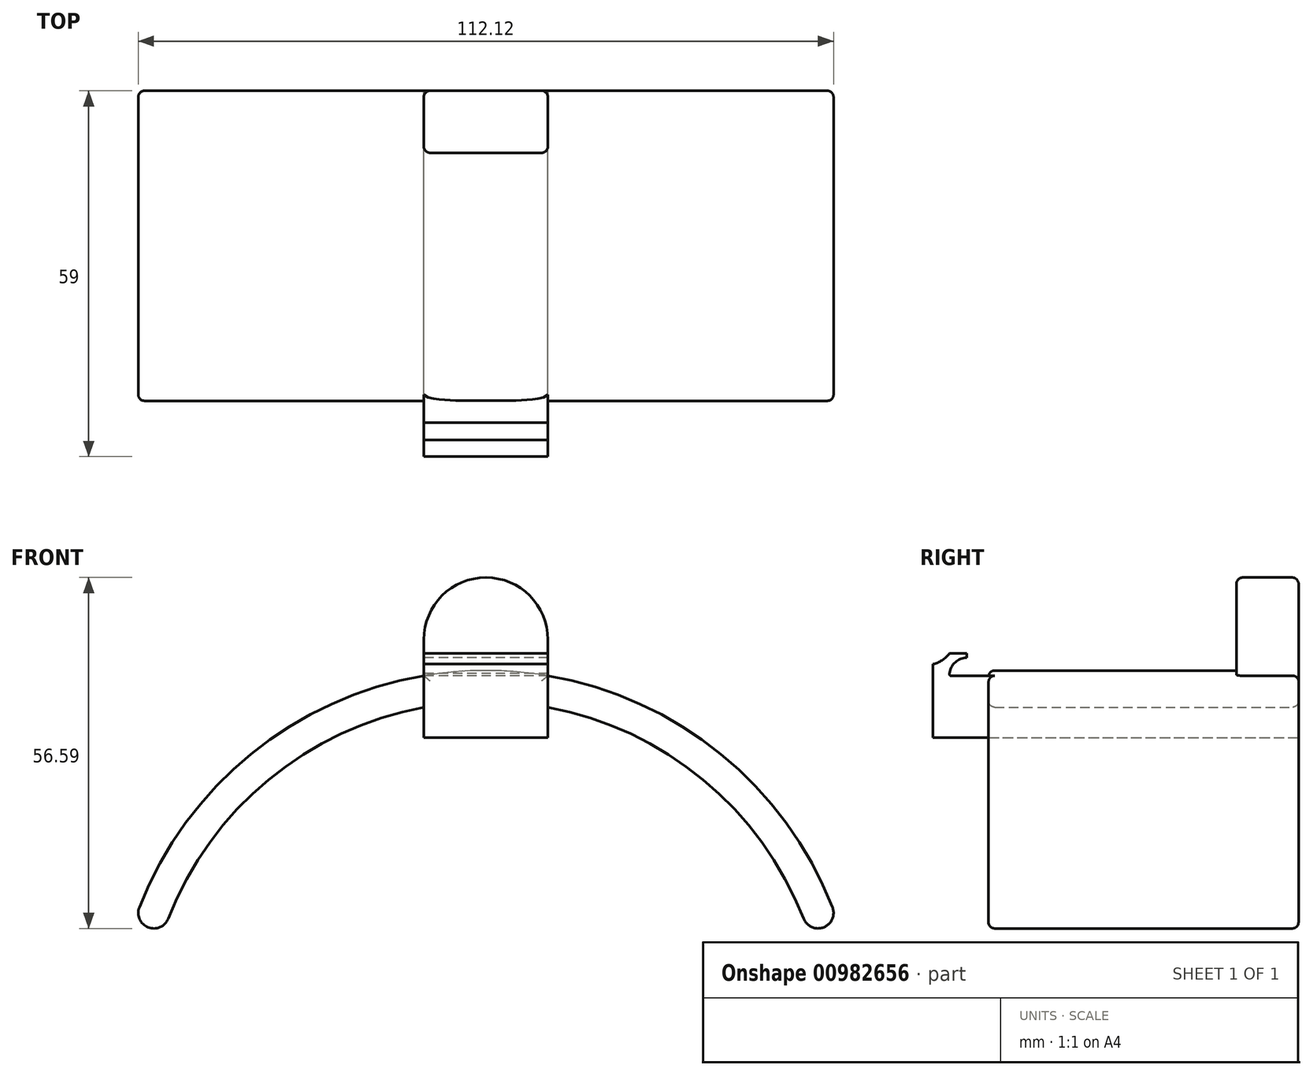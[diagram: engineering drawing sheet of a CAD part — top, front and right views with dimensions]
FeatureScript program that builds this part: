
annotation { "Feature Type Name" : "Feature", "Feature Type Description" : "" }
export const myFeature = defineFeature(function(context is Context, id is Id, definition is map)
    precondition{}
    {
        {
            var Q0;
            Q0=qCreatedBy(makeId("Right.planeOp"),FACE);
            var sketch = newSketch(context, id + "F0", { "sketchPlane" : qUnion([Q0])});
            skLineSegment(sketch, "E0.bottom", {"start": v(2.7, 2.31) * mm, "end": v(5.5, 2.31) * mm});
            skLineSegment(sketch, "E0.right", {"start": v(5.5, 2.31) * mm, "end": v(5.5, 1.65) * mm});
            skLineSegment(sketch, "E1", {"start": v(2.7, -1.07) * mm, "end": v(2.7, -0.9) * mm});
            skLineSegment(sketch, "E2.top", {"start": v(0, -11.29) * mm, "end": v(9, -11.29) * mm});
            skLineSegment(sketch, "E2.right", {"start": v(9, -1.29) * mm, "end": v(9, -11.29) * mm});
            skLineSegment(sketch, "E3", {"start": v(2.92, -1.29) * mm, "end": v(9, -1.29) * mm});
            skArc(sketch, "E4", {"start": v(0, 0.58) * mm, "mid": v(1.5, 1.2) * mm, "end": v(2.7, 2.31) * mm});
            skPoint(sketch, "E5.visualSharp", {"position": v(2.7, -1.29) * mm});
            skArc(sketch, "E5.filletArc", {"start": v(2.7, -1.07) * mm, "mid": v(2.76, -1.22) * mm, "end": v(2.92, -1.29) * mm});
            skArc(sketch, "E6", {"start": v(5.5, 1.65) * mm, "mid": v(3.63, 0.89) * mm, "end": v(2.7, -0.9) * mm});
            skLineSegment(sketch, "E7", {"start": v(0, 0.58) * mm, "end": v(0, -11.29) * mm});
            skLineSegment(sketch, "E8", {"start": v(2.7, -0.9) * mm, "end": v(2.7, 6.55) * mm, "construction": true});
            skSolve(sketch);
        }
        {
            var Q0;
            Q0=qSketchRegion(id+"F0",true);
            extrude(context, id + "F1", {"entities" : qUnion([Q0]), "depth" : 20 * mm, "offsetDistance" : 25.4 * mm});
        }
        {
            var Q0;
            Q0=qCreatedBy(makeId("Right.planeOp"),FACE);
            var sketch = newSketch(context, id + "F2", { "sketchPlane" : qUnion([Q0])});
            skLineSegment(sketch, "E9.top", {"start": v(9, -1.29) * mm, "end": v(59, -1.29) * mm});
            skLineSegment(sketch, "E9.right", {"start": v(59, -11.29) * mm, "end": v(59, -1.29) * mm});
            skPoint(sketch, "E10", {"position": v(9, -11.29) * mm});
            skLineSegment(sketch, "E11", {"start": v(59, -11.29) * mm, "end": v(9, -11.29) * mm});
            skLineSegment(sketch, "E12", {"start": v(9, -11.29) * mm, "end": v(9, -1.29) * mm});
            skSolve(sketch);
        }
        {
            var Q0;
            Q0 = qSketchRegion(id + "F2", true);
            extrude(context, id + "F3", {"entities" : qUnion([Q0]), "operationType" : NewBodyOperationType.ADD, "depth" : 20 * mm, "offsetDistance" : 25.4 * mm});
        }
        {
            var Q0;
            Q0=makeQuery(id+"F3.opExtrude","SWEPT_FACE",FACE,{"disambiguationData":[OSD([sQuery(id+"F2.wireOp",EDGE,"E9.right")])]});
            cPlane(context, id + "F4", {"entities" : qUnion([Q0]), "cplaneType" : CPlaneType.OFFSET, "offset" : 0 * mm, "width" : 152.4 * mm, "height" : 152.4 * mm});
        }
        {
            var Q0;
            Q0=qCreatedBy(id+"F4.planeOp",FACE);
            var sketch = newSketch(context, id + "F5", { "sketchPlane" : qUnion([Q0])});
            skArc(sketch, "E13", {"start": v(45.9, -38.63) * mm, "mid": v(-10, -0.45) * mm, "end": v(-65.9, -38.63) * mm});
            skArc(sketch, "E14", {"start": v(41.23, -40.45) * mm, "mid": v(-10, -5.45) * mm, "end": v(-61.23, -40.45) * mm});
            skLineSegment(sketch, "E15", {"start": v(-10, -60.45) * mm, "end": v(-61.23, -40.45) * mm, "construction": true});
            skLineSegment(sketch, "E16", {"start": v(-10, -60.45) * mm, "end": v(41.23, -40.45) * mm, "construction": true});
            skLineSegment(sketch, "E17", {"start": v(41.23, -40.45) * mm, "end": v(-69.72, -40.45) * mm, "construction": true});
            skArc(sketch, "E18", {"start": v(-65.9, -38.63) * mm, "mid": v(-64.47, -41.87) * mm, "end": v(-61.23, -40.45) * mm});
            skArc(sketch, "E19", {"start": v(41.23, -40.45) * mm, "mid": v(44.47, -41.87) * mm, "end": v(45.9, -38.63) * mm});
            skSolve(sketch);
        }
        {
            var Q0;
            Q0 = qSketchRegion(id + "F5", true);
            extrude(context, id + "F6", {"entities" : qUnion([Q0]), "operationType" : NewBodyOperationType.ADD, "oppositeDirection" : true, "depth" : 50 * mm, "offsetDistance" : 25.4 * mm});
        }
        {
            var Q0;
            {var subQ0=sQuery(id+"F2.wireOp",EDGE,"E9.top");var subQ1=sQuery(id+"F0.wireOp",EDGE,"E3");var subQ2=sQuery(id+"F5.wireOp",EDGE,"E18");var subQ3=sQuery(id+"F5.wireOp",EDGE,"E13");Q0=makeQuery(id+"F6.boolean.opBoolean","SPLIT",EDGE,{"disambiguationData":[TD([makeQuery(id+"F1.opExtrude","CAP_FACE",FACE,{"disambiguationData":[OSD([sQuery(id+"F0.wireOp",EDGE,"E0.bottom"),sQuery(id+"F0.wireOp",EDGE,"E0.right"),sQuery(id+"F0.wireOp",EDGE,"E1"),sQuery(id+"F0.wireOp",EDGE,"E2.top"),sQuery(id+"F0.wireOp",EDGE,"E2.right"),subQ1,sQuery(id+"F0.wireOp",EDGE,"E4"),sQuery(id+"F0.wireOp",EDGE,"E5.filletArc"),sQuery(id+"F0.wireOp",EDGE,"E6"),sQuery(id+"F0.wireOp",EDGE,"E7")])],"isStart":false}),makeQuery(id+"F1.opExtrude","SWEPT_FACE",FACE,{"disambiguationData":[OSD([subQ1])]}),makeQuery(id+"F3.opExtrude","SWEPT_FACE",FACE,{"disambiguationData":[OSD([subQ0])]}),makeQuery(id+"F3.opExtrude","CAP_FACE",FACE,{"disambiguationData":[OSD([subQ0,sQuery(id+"F2.wireOp",EDGE,"E9.right"),sQuery(id+"F2.wireOp",EDGE,"E11"),sQuery(id+"F2.wireOp",EDGE,"E12")])],"isStart":false}),makeQuery(id+"F6.opExtrude","SWEPT_FACE",FACE,{"disambiguationData":[OSD([subQ3])]}),makeQuery(id+"F6.opExtrude","CAP_FACE",FACE,{"disambiguationData":[OSD([subQ3,sQuery(id+"F5.wireOp",EDGE,"E14"),subQ2,sQuery(id+"F5.wireOp",EDGE,"E19")])],"isStart":false}),makeQuery(id+"F6.opExtrude","SWEPT_FACE",FACE,{"disambiguationData":[OSD([subQ2])]})])],"derivedFrom":makeQuery(id+"F6.opExtrude","CAP_EDGE",EDGE,{"disambiguationData":[OSD([subQ3])],"isStart":false})});}
            fillet(context, id + "F7", {"entities" : qUnion([Q0]), "radius" : 1 * mm, "tangentPropagation" : true, "allowEdgeOverflow" : false});
        }
        {
            var Q0;
            Q0=qCreatedBy(id+"F4.planeOp",FACE);
            var sketch = newSketch(context, id + "F8", { "sketchPlane" : qUnion([Q0])});
            skLineSegment(sketch, "E20.bottom", {"start": v(-20, -11.29) * mm, "end": v(0, -11.29) * mm});
            skLineSegment(sketch, "E20.top", {"start": v(-10, 14.55) * mm, "end": v(-10, 14.55) * mm});
            skLineSegment(sketch, "E20.left", {"start": v(-20, -11.29) * mm, "end": v(-20, 4.55) * mm});
            skLineSegment(sketch, "E20.right", {"start": v(0, -11.29) * mm, "end": v(0, 4.55) * mm});
            skPoint(sketch, "E21.visualSharp", {"position": v(-20, 14.55) * mm});
            skArc(sketch, "E21.filletArc", {"start": v(-10, 14.55) * mm, "mid": v(-17.07, 11.62) * mm, "end": v(-20, 4.55) * mm});
            skPoint(sketch, "E22.visualSharp", {"position": v(0, 14.55) * mm});
            skArc(sketch, "E22.filletArc", {"start": v(0, 4.55) * mm, "mid": v(-2.93, 11.62) * mm, "end": v(-10, 14.55) * mm});
            skSolve(sketch);
        }
        {
            var Q0;
            Q0 = qSketchRegion(id + "F8", true);
            extrude(context, id + "F9", {"entities" : qUnion([Q0]), "operationType" : NewBodyOperationType.ADD, "oppositeDirection" : true, "depth" : 10 * mm, "offsetDistance" : 25.4 * mm});
        }
        {
            var Q0;
            {var subQ0=sQuery(id+"F2.wireOp",EDGE,"E9.top");var subQ1=sQuery(id+"F5.wireOp",EDGE,"E13");var subQ2=sQuery(id+"F0.wireOp",EDGE,"E3");var subQ3=sQuery(id+"F2.wireOp",EDGE,"E12");var subQ4=sQuery(id+"F2.wireOp",EDGE,"E11");var subQ5=sQuery(id+"F2.wireOp",EDGE,"E9.right");var subQ6=sQuery(id+"F0.wireOp",EDGE,"E7");var subQ7=sQuery(id+"F0.wireOp",EDGE,"E6");var subQ8=sQuery(id+"F0.wireOp",EDGE,"E5.filletArc");var subQ9=sQuery(id+"F0.wireOp",EDGE,"E4");var subQ10=sQuery(id+"F0.wireOp",EDGE,"E2.right");var subQ11=sQuery(id+"F0.wireOp",EDGE,"E2.top");var subQ12=sQuery(id+"F0.wireOp",EDGE,"E1");var subQ13=sQuery(id+"F0.wireOp",EDGE,"E0.right");var subQ14=sQuery(id+"F0.wireOp",EDGE,"E0.bottom");Q0=makeQuery(id+"F6.boolean.opBoolean","SPLIT",EDGE,{"disambiguationData":[TD([makeQuery(id+"F1.opExtrude","CAP_FACE",FACE,{"disambiguationData":[OSD([subQ14,subQ13,subQ12,subQ11,subQ10,subQ2,subQ9,subQ8,subQ7,subQ6])],"isStart":true}),makeQuery(id+"F1.opExtrude","CAP_FACE",FACE,{"disambiguationData":[OSD([subQ14,subQ13,subQ12,subQ11,subQ10,subQ2,subQ9,subQ8,subQ7,subQ6])],"isStart":false}),makeQuery(id+"F1.opExtrude","SWEPT_FACE",FACE,{"disambiguationData":[OSD([subQ2])]}),makeQuery(id+"F3.opExtrude","SWEPT_FACE",FACE,{"disambiguationData":[OSD([subQ0])]}),makeQuery(id+"F3.opExtrude","CAP_FACE",FACE,{"disambiguationData":[OSD([subQ0,subQ5,subQ4,subQ3])],"isStart":true}),makeQuery(id+"F3.opExtrude","CAP_FACE",FACE,{"disambiguationData":[OSD([subQ0,subQ5,subQ4,subQ3])],"isStart":false}),makeQuery(id+"F6.opExtrude","SWEPT_FACE",FACE,{"disambiguationData":[OSD([subQ1])]}),makeQuery(id+"F6.opExtrude","CAP_FACE",FACE,{"disambiguationData":[OSD([subQ1,sQuery(id+"F5.wireOp",EDGE,"E14"),sQuery(id+"F5.wireOp",EDGE,"E18"),sQuery(id+"F5.wireOp",EDGE,"E19")])],"isStart":false})])],"derivedFrom":makeQuery(id+"F6.opExtrude","CAP_EDGE",EDGE,{"disambiguationData":[OSD([subQ1])],"isStart":false})});}
            fillet(context, id + "F10", {"entities" : qUnion([Q0]), "radius" : 1 * mm, "tangentPropagation" : true, "allowEdgeOverflow" : false});
        }
        {
            var Q0;
            {var subQ0=sQuery(id+"F5.wireOp",EDGE,"E18");var subQ1=sQuery(id+"F5.wireOp",EDGE,"E13");Q0=makeQuery(id+"F9.boolean.opBoolean","SPLIT",EDGE,{"disambiguationData":[TD([makeQuery(id+"F6.opExtrude","SWEPT_FACE",FACE,{"disambiguationData":[OSD([subQ0])]})])],"derivedFrom":makeQuery(id+"F6.opExtrude","CAP_EDGE",EDGE,{"disambiguationData":[OSD([subQ1])],"isStart":true})});}
            var Q1;
            {var subQ0=sQuery(id+"F5.wireOp",EDGE,"E19");var subQ1=sQuery(id+"F5.wireOp",EDGE,"E13");Q1=makeQuery(id+"F9.boolean.opBoolean","SPLIT",EDGE,{"disambiguationData":[TD([makeQuery(id+"F6.opExtrude","SWEPT_FACE",FACE,{"disambiguationData":[OSD([subQ0])]})])],"derivedFrom":makeQuery(id+"F6.opExtrude","CAP_EDGE",EDGE,{"disambiguationData":[OSD([subQ1])],"isStart":true})});}
            var Q2;
            {var subQ0=sQuery(id+"F8.wireOp",EDGE,"E22.filletArc");var subQ1=sQuery(id+"F8.wireOp",EDGE,"E21.filletArc");Q2=makeQuery(id+"FTdjPDUJ5qywCfE_2.opFillet","BLEND_FACE",FACE,{"disambiguationData":[OSD([subQ1,subQ0]),TDD([makeQuery(id+"F9.opExtrude","CAP_EDGE",EDGE,{"disambiguationData":[OSD([subQ1,subQ0])],"isStart":true})])]});}
            var Q3;
            {var subQ0=sQuery(id+"F8.wireOp",EDGE,"E22.filletArc");var subQ1=sQuery(id+"F8.wireOp",EDGE,"E21.filletArc");Q3=makeQuery(id+"FTdjPDUJ5qywCfE_2.opFillet","BLEND_FACE",FACE,{"disambiguationData":[OSD([subQ1,subQ0]),TDD([makeQuery(id+"F9.opExtrude","CAP_EDGE",EDGE,{"disambiguationData":[OSD([subQ1,subQ0])],"isStart":false})])]});}
            fillet(context, id + "F11", {"entities" : qUnion([Q0, Q1, Q2, Q3]), "radius" : 1 * mm, "tangentPropagation" : true, "allowEdgeOverflow" : false});
        }
        {
            var Q0;
            Q0=makeQuery(id+"F9.opExtrude","CAP_EDGE",EDGE,{"disambiguationData":[OSD([sQuery(id+"F8.wireOp",EDGE,"E21.filletArc"),sQuery(id+"F8.wireOp",EDGE,"E22.filletArc")])],"isStart":true});
            var Q1;
            Q1=makeQuery(id+"F9.opExtrude","CAP_EDGE",EDGE,{"disambiguationData":[OSD([sQuery(id+"F8.wireOp",EDGE,"E21.filletArc"),sQuery(id+"F8.wireOp",EDGE,"E22.filletArc")])],"isStart":false});
            fillet(context, id + "F12", {"entities" : qUnion([Q0, Q1]), "radius" : 1 * mm, "tangentPropagation" : true, "allowEdgeOverflow" : false});
        }
    });
